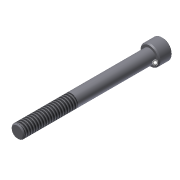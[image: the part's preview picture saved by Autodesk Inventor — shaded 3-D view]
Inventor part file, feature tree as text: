
AUTODESK INVENTOR PART (.ipt)
format: ipt  version: 2013 (Build 170138000, 138)  size: 101,888 bytes
history: native  units: in
note: dims shown in document units (in); Inventor stores cm internally (conversion verified against a paired STEP export)
features: extrude x3, sketch x3, chamfer x1, thread x1
ambient origin geometry x8: Origin, YZ Plane, XZ Plane, XY Plane, X Axis, Y Axis, Z Axis, Center Point
bodies: Solid1 (feature_tree)
feature tree (8):
  extrude  "Extrusion1"  Depth=2.5in TaperAngle=0.0deg
  extrude  "Extrusion2"  Depth=0.25in TaperAngle=0.0deg
  extrude  "Extrusion3"  Depth=0.125in TaperAngle=0.0deg
  chamfer  "Chamfer1"  Distance=0.02in Angle=45.0deg
  thread  "Thread1"  [1 undecoded]
  sketch  "Sketch1"  dims[d0=0.25in d1=2.5in d2=0.0in]
  sketch  "Sketch2"  dims[d3=0.375in d4=0.25in d5=0.0in]
  sketch  "Sketch3"  dims[d6=0.1875in d7=0.125in d8=0.0in d9=0.02in d10=0.125in d11=45.0deg d12=1.0in d13=0.0in d14=0.0in]
note: 1 required parameter value undecoded (feature->parameter linkage not recoverable at this tier; creation-order binding heuristic only, values carry confidence <= 0.55)
